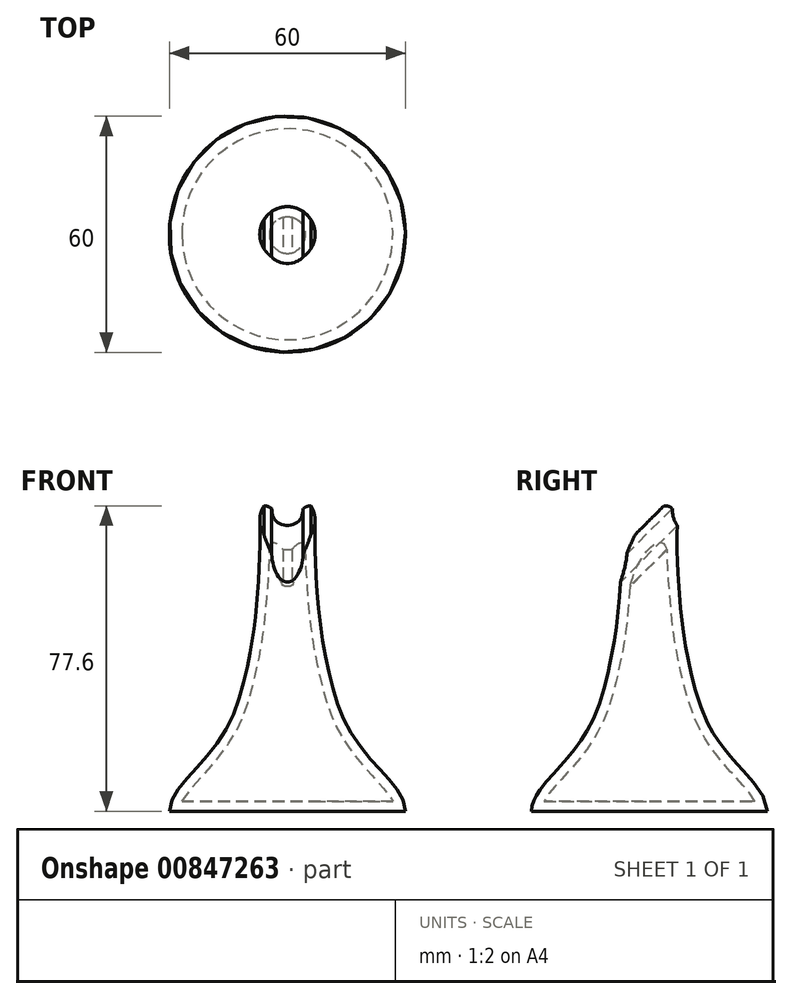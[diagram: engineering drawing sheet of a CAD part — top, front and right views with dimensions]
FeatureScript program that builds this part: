
annotation { "Feature Type Name" : "Feature", "Feature Type Description" : "" }
export const myFeature = defineFeature(function(context is Context, id is Id, definition is map)
    precondition{}
    {
        {
            var Q0;
            Q0=qCreatedBy(makeId("Front.planeOp"),FACE);
            var sketch = newSketch(context, id + "F0", { "sketchPlane" : qUnion([Q0])});
            skLineSegment(sketch, "E0", {"start": v(0, 0) * mm, "end": v(0, 83.4) * mm, "construction": true});
            skLineSegment(sketch, "E1", {"start": v(0, 78) * mm, "end": v(0, 0) * mm});
            skLineSegment(sketch, "E2", {"start": v(0, 78) * mm, "end": v(7, 78) * mm});
            skLineSegment(sketch, "E3", {"start": v(0, 0) * mm, "end": v(30, 0) * mm});
            skFitSpline(sketch, "E4", {"points": [v(7, 78) * mm, v(7, 66.05) * mm, v(8.2, 48.7) * mm, v(10.23, 36.7) * mm, v(12.9, 26.8) * mm, v(17.2, 18.3) * mm, v(24.46, 9.5) * mm, v(30, 0) * mm], "startDerivative": vector(1.84, -191.92) * mm, "endDerivative": vector(-0.05, -76.6) * mm});
            skSolve(sketch);
        }
        {
            var Q0;
            Q0=makeQuery(id+"F0.imprint","IMPRINT",FACE,{"disambiguationData":[TD([[makeQuery(id+"F0.imprint","IMPRINT",EDGE,{"derivedFrom":sQuery(id+"F0.wireOp",EDGE,"E1")}),1.0]])]});
            var Q1;
            Q1=sQuery(id+"F0.wireOp",EDGE,"E0");
            revolve(context, id + "F1", {"surfaceOperationType" : NewSurfaceOperationType.NEW, "entities" : qUnion([Q0]), "axis" : qUnion([Q1]), "revolveType" : RevolveType.FULL});
        }
        {
            var Q0;
            Q0=qCreatedBy(makeId("Front.planeOp"),FACE);
            var Q1;
            Q1=qCreatedBy(makeId("Top.planeOp"),FACE);
            cPlane(context, id + "F2", {"entities" : qUnion([Q0, Q1]), "cplaneType" : CPlaneType.MID_PLANE, "offset" : 25 * mm, "width" : 150 * mm, "height" : 150 * mm});
        }
        {
            var Q0;
            Q0=qCreatedBy(id+"F2.planeOp",FACE);
            var sketch = newSketch(context, id + "F3", { "sketchPlane" : qUnion([Q0])});
            skLineSegment(sketch, "E5", {"start": v(-8.64, 52.3) * mm, "end": v(-4, 52.3) * mm});
            skArc(sketch, "E6", {"start": v(-4, 50.38) * mm, "mid": v(0, 46.38) * mm, "end": v(4, 50.38) * mm});
            skLineSegment(sketch, "E7", {"start": v(-4, 50.38) * mm, "end": v(-4, 52.3) * mm});
            skLineSegment(sketch, "E8", {"start": v(4, 50.38) * mm, "end": v(4, 52.3) * mm});
            skLineSegment(sketch, "E9", {"start": v(-8.64, 52.3) * mm, "end": v(-8.64, 61.01) * mm});
            skLineSegment(sketch, "E10", {"start": v(-8.64, 61.01) * mm, "end": v(8.47, 61.01) * mm});
            skLineSegment(sketch, "E11", {"start": v(8.47, 61.01) * mm, "end": v(7.86, 52.3) * mm});
            skLineSegment(sketch, "E12.trimOffspring", {"start": v(4, 52.3) * mm, "end": v(7.86, 52.3) * mm});
            skSolve(sketch);
        }
        {
            var Q0;
            Q0=makeQuery(id+"F3.imprint","IMPRINT",FACE,{"disambiguationData":[TD([[makeQuery(id+"F3.imprint","IMPRINT",EDGE,{"derivedFrom":sQuery(id+"F3.wireOp",EDGE,"E5")}),1.0]])]});
            extrude(context, id + "F4", {"entities" : qUnion([Q0]), "operationType" : NewBodyOperationType.REMOVE, "oppositeDirection" : true, "depth" : 65 * mm, "offsetDistance" : 25 * mm});
        }
        {
            var Q0;
            Q0=makeQuery(id+"F4.boolean.opBoolean","COPY",EDGE,{"derivedFrom":makeQuery(id+"F4.opExtrude","SWEPT_EDGE",EDGE,{"disambiguationData":[OSD([sQuery(id+"F3.wireOp",EDGE,"E5"),sQuery(id+"F3.wireOp",EDGE,"E7")])]})});
            var Q1;
            Q1=makeQuery(id+"F4.boolean.opBoolean","COPY",EDGE,{"derivedFrom":makeQuery(id+"F4.opExtrude","SWEPT_EDGE",EDGE,{"disambiguationData":[OSD([sQuery(id+"F3.wireOp",EDGE,"E8"),sQuery(id+"F3.wireOp",EDGE,"E12.trimOffspring")])]})});
            chamfer(context, id + "F5", {"entities" : qUnion([Q0, Q1]), "width" : 2 * mm, "tangentPropagation" : true});
        }
        {
            var Q0;
            Q0=makeQuery(id+"F4.boolean.opBoolean","COPY",FACE,{"derivedFrom":makeQuery(id+"F4.opExtrude","SWEPT_FACE",FACE,{"disambiguationData":[OSD([sQuery(id+"F3.wireOp",EDGE,"E12.trimOffspring")])]})});
            var Q1;
            Q1=makeQuery(id+"F4.boolean.opBoolean","COPY",FACE,{"derivedFrom":makeQuery(id+"F4.opExtrude","SWEPT_FACE",FACE,{"disambiguationData":[OSD([sQuery(id+"F3.wireOp",EDGE,"E5")])]})});
            shell(context, id + "F6", {"entities" : qUnion([Q0, Q1]), "thickness" : 2.5 * mm});
        }
    });
